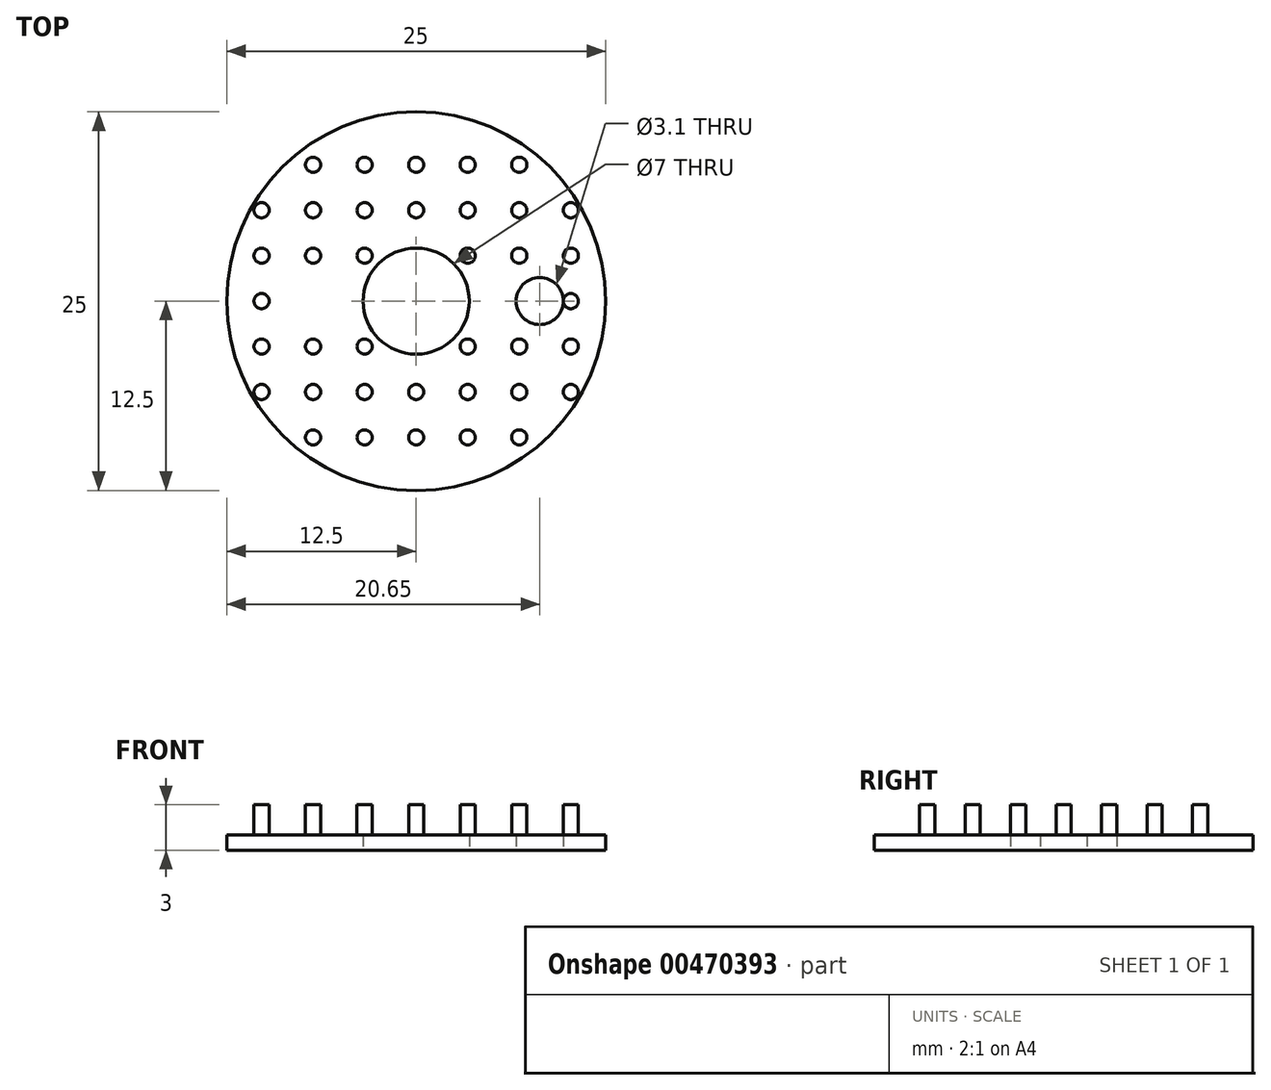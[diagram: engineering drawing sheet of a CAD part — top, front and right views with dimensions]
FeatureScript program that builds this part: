
annotation { "Feature Type Name" : "Feature", "Feature Type Description" : "" }
export const myFeature = defineFeature(function(context is Context, id is Id, definition is map)
    precondition{}
    {
        {
            var Q0;
            Q0=qCreatedBy(makeId("Top.planeOp"),FACE);
            var sketch = newSketch(context, id + "F0", { "sketchPlane" : qUnion([Q0])});
            skCircle(sketch, "E0", {"center": v(0, 0) * mm, "radius": 12.5 * mm});
            skSolve(sketch);
        }
        {
            var Q0;
            Q0=makeQuery(id+"F0.imprint","IMPRINT",FACE,{"disambiguationData":[TD([[makeQuery(id+"F0.imprint","IMPRINT",EDGE,{"derivedFrom":sQuery(id+"F0.wireOp",EDGE,"E0")}),1.0]])]});
            extrude(context, id + "F1", {"entities" : qUnion([Q0]), "depth" : 1 * mm, "offsetDistance" : 25 * mm});
        }
        {
            var Q0;
            Q0=qCreatedBy(makeId("Top.planeOp"),FACE);
            var sketch = newSketch(context, id + "F2", { "sketchPlane" : qUnion([Q0])});
            skCircle(sketch, "E1", {"center": v(-10.2, -12) * mm, "radius": 0.5 * mm});
            skLineSegment(sketch, "E2.direction1", {"start": v(-10.2, -12) * mm, "end": v(-6.8, -12) * mm, "construction": true});
            skLineSegment(sketch, "E2.direction2", {"start": v(-10.2, -12) * mm, "end": v(-10.2, -9) * mm, "construction": true});
            skCircle(sketch, "E3.0.0.1", {"center": v(-10.2, -9) * mm, "radius": 0.5 * mm});
            skCircle(sketch, "E3.0.0.2", {"center": v(-10.2, -6) * mm, "radius": 0.5 * mm});
            skCircle(sketch, "E3.0.0.3", {"center": v(-10.2, -3) * mm, "radius": 0.5 * mm});
            skCircle(sketch, "E3.0.0.4", {"center": v(-10.2, 0) * mm, "radius": 0.5 * mm});
            skCircle(sketch, "E3.0.0.5", {"center": v(-10.2, 3) * mm, "radius": 0.5 * mm});
            skCircle(sketch, "E3.0.0.6", {"center": v(-10.2, 6) * mm, "radius": 0.5 * mm});
            skCircle(sketch, "E4.0.1.0", {"center": v(-6.8, -12) * mm, "radius": 0.5 * mm});
            skCircle(sketch, "E4.0.1.1", {"center": v(-6.8, -9) * mm, "radius": 0.5 * mm});
            skCircle(sketch, "E4.0.1.2", {"center": v(-6.8, -6) * mm, "radius": 0.5 * mm});
            skCircle(sketch, "E4.0.1.3", {"center": v(-6.8, -3) * mm, "radius": 0.5 * mm});
            skCircle(sketch, "E4.0.1.4", {"center": v(-6.8, 0) * mm, "radius": 0.5 * mm});
            skCircle(sketch, "E4.0.1.5", {"center": v(-6.8, 3) * mm, "radius": 0.5 * mm});
            skCircle(sketch, "E4.0.1.6", {"center": v(-6.8, 6) * mm, "radius": 0.5 * mm});
            skCircle(sketch, "E4.0.2.1", {"center": v(-3.4, -9) * mm, "radius": 0.5 * mm});
            skCircle(sketch, "E4.0.2.2", {"center": v(-3.4, -6) * mm, "radius": 0.5 * mm});
            skCircle(sketch, "E4.0.2.3", {"center": v(-3.4, -3) * mm, "radius": 0.5 * mm});
            skCircle(sketch, "E4.0.2.4", {"center": v(-3.4, 0) * mm, "radius": 0.5 * mm});
            skCircle(sketch, "E4.0.2.5", {"center": v(-3.4, 3) * mm, "radius": 0.5 * mm});
            skCircle(sketch, "E4.0.2.6", {"center": v(-3.4, 6) * mm, "radius": 0.5 * mm});
            skCircle(sketch, "E4.0.3.1", {"center": v(0, -9) * mm, "radius": 0.5 * mm});
            skCircle(sketch, "E4.0.3.2", {"center": v(0, -6) * mm, "radius": 0.5 * mm});
            skCircle(sketch, "E4.0.3.3", {"center": v(0, -3) * mm, "radius": 0.5 * mm});
            skCircle(sketch, "E4.0.3.4", {"center": v(0, 0) * mm, "radius": 0.5 * mm});
            skCircle(sketch, "E4.0.3.5", {"center": v(0, 3) * mm, "radius": 0.5 * mm});
            skCircle(sketch, "E4.0.3.6", {"center": v(0, 6) * mm, "radius": 0.5 * mm});
            skCircle(sketch, "E4.0.4.1", {"center": v(3.4, -9) * mm, "radius": 0.5 * mm});
            skCircle(sketch, "E4.0.4.2", {"center": v(3.4, -6) * mm, "radius": 0.5 * mm});
            skCircle(sketch, "E4.0.4.3", {"center": v(3.4, -3) * mm, "radius": 0.5 * mm});
            skCircle(sketch, "E4.0.4.4", {"center": v(3.4, 0) * mm, "radius": 0.5 * mm});
            skCircle(sketch, "E4.0.4.5", {"center": v(3.4, 3) * mm, "radius": 0.5 * mm});
            skCircle(sketch, "E4.0.4.6", {"center": v(3.4, 6) * mm, "radius": 0.5 * mm});
            skCircle(sketch, "E4.0.5.1", {"center": v(6.8, -9) * mm, "radius": 0.5 * mm});
            skCircle(sketch, "E4.0.5.2", {"center": v(6.8, -6) * mm, "radius": 0.5 * mm});
            skCircle(sketch, "E4.0.5.3", {"center": v(6.8, -3) * mm, "radius": 0.5 * mm});
            skCircle(sketch, "E4.0.5.4", {"center": v(6.8, 0) * mm, "radius": 0.5 * mm});
            skCircle(sketch, "E4.0.5.5", {"center": v(6.8, 3) * mm, "radius": 0.5 * mm});
            skCircle(sketch, "E4.0.5.6", {"center": v(6.8, 6) * mm, "radius": 0.5 * mm});
            skCircle(sketch, "E4.0.6.2", {"center": v(10.2, -6) * mm, "radius": 0.5 * mm});
            skCircle(sketch, "E4.0.6.3", {"center": v(10.2, -3) * mm, "radius": 0.5 * mm});
            skCircle(sketch, "E4.0.6.4", {"center": v(10.2, 0) * mm, "radius": 0.5 * mm});
            skCircle(sketch, "E4.0.6.5", {"center": v(10.2, 3) * mm, "radius": 0.5 * mm});
            skCircle(sketch, "E4.0.6.6", {"center": v(10.2, 6) * mm, "radius": 0.5 * mm});
            skCircle(sketch, "E5.0.1.7", {"center": v(-6.8, 9) * mm, "radius": 0.5 * mm});
            skCircle(sketch, "E5.0.2.7", {"center": v(-3.4, 9) * mm, "radius": 0.5 * mm});
            skCircle(sketch, "E5.0.3.7", {"center": v(0, 9) * mm, "radius": 0.5 * mm});
            skCircle(sketch, "E5.0.4.7", {"center": v(3.4, 9) * mm, "radius": 0.5 * mm});
            skCircle(sketch, "E5.0.5.7", {"center": v(6.8, 9) * mm, "radius": 0.5 * mm});
            skSolve(sketch);
        }
        {
            var Q0;
            Q0=makeQuery(id+"F2.imprint","IMPRINT",FACE,{"disambiguationData":[TD([[makeQuery(id+"F2.imprint","IMPRINT",EDGE,{"derivedFrom":sQuery(id+"F2.wireOp",EDGE,"E4.0.6.5")}),1.0]])]});
            var Q1;
            Q1=makeQuery(id+"F2.imprint","IMPRINT",FACE,{"disambiguationData":[TD([[makeQuery(id+"F2.imprint","IMPRINT",EDGE,{"derivedFrom":sQuery(id+"F2.wireOp",EDGE,"E4.0.5.6")}),1.0]])]});
            var Q2;
            Q2=makeQuery(id+"F2.imprint","IMPRINT",FACE,{"disambiguationData":[TD([[makeQuery(id+"F2.imprint","IMPRINT",EDGE,{"derivedFrom":sQuery(id+"F2.wireOp",EDGE,"E4.0.6.4")}),1.0]])]});
            var Q3;
            Q3=makeQuery(id+"F2.imprint","IMPRINT",FACE,{"disambiguationData":[TD([[makeQuery(id+"F2.imprint","IMPRINT",EDGE,{"derivedFrom":sQuery(id+"F2.wireOp",EDGE,"E4.0.6.3")}),1.0]])]});
            var Q4;
            Q4=makeQuery(id+"F2.imprint","IMPRINT",FACE,{"disambiguationData":[TD([[makeQuery(id+"F2.imprint","IMPRINT",EDGE,{"derivedFrom":sQuery(id+"F2.wireOp",EDGE,"E4.0.5.2")}),1.0]])]});
            var Q5;
            Q5=makeQuery(id+"F2.imprint","IMPRINT",FACE,{"disambiguationData":[TD([[makeQuery(id+"F2.imprint","IMPRINT",EDGE,{"derivedFrom":sQuery(id+"F2.wireOp",EDGE,"E4.0.4.2")}),1.0]])]});
            var Q6;
            Q6=makeQuery(id+"F2.imprint","IMPRINT",FACE,{"disambiguationData":[TD([[makeQuery(id+"F2.imprint","IMPRINT",EDGE,{"derivedFrom":sQuery(id+"F2.wireOp",EDGE,"E4.0.3.2")}),1.0]])]});
            var Q7;
            Q7=makeQuery(id+"F2.imprint","IMPRINT",FACE,{"disambiguationData":[TD([[makeQuery(id+"F2.imprint","IMPRINT",EDGE,{"derivedFrom":sQuery(id+"F2.wireOp",EDGE,"E4.0.2.2")}),1.0]])]});
            var Q8;
            Q8=makeQuery(id+"F2.imprint","IMPRINT",FACE,{"disambiguationData":[TD([[makeQuery(id+"F2.imprint","IMPRINT",EDGE,{"derivedFrom":sQuery(id+"F2.wireOp",EDGE,"E4.0.1.2")}),1.0]])]});
            var Q9;
            Q9=makeQuery(id+"F2.imprint","IMPRINT",FACE,{"disambiguationData":[TD([[makeQuery(id+"F2.imprint","IMPRINT",EDGE,{"derivedFrom":sQuery(id+"F2.wireOp",EDGE,"E3.0.0.3")}),1.0]])]});
            var Q10;
            Q10=makeQuery(id+"F2.imprint","IMPRINT",FACE,{"disambiguationData":[TD([[makeQuery(id+"F2.imprint","IMPRINT",EDGE,{"derivedFrom":sQuery(id+"F2.wireOp",EDGE,"E3.0.0.4")}),1.0]])]});
            var Q11;
            Q11=makeQuery(id+"F2.imprint","IMPRINT",FACE,{"disambiguationData":[TD([[makeQuery(id+"F2.imprint","IMPRINT",EDGE,{"derivedFrom":sQuery(id+"F2.wireOp",EDGE,"E3.0.0.5")}),1.0]])]});
            var Q12;
            Q12=makeQuery(id+"F2.imprint","IMPRINT",FACE,{"disambiguationData":[TD([[makeQuery(id+"F2.imprint","IMPRINT",EDGE,{"derivedFrom":sQuery(id+"F2.wireOp",EDGE,"E4.0.1.6")}),1.0]])]});
            var Q13;
            Q13=makeQuery(id+"F2.imprint","IMPRINT",FACE,{"disambiguationData":[TD([[makeQuery(id+"F2.imprint","IMPRINT",EDGE,{"derivedFrom":sQuery(id+"F2.wireOp",EDGE,"E4.0.2.6")}),1.0]])]});
            var Q14;
            Q14=makeQuery(id+"F2.imprint","IMPRINT",FACE,{"disambiguationData":[TD([[makeQuery(id+"F2.imprint","IMPRINT",EDGE,{"derivedFrom":sQuery(id+"F2.wireOp",EDGE,"E4.0.3.6")}),1.0]])]});
            var Q15;
            Q15=makeQuery(id+"F2.imprint","IMPRINT",FACE,{"disambiguationData":[TD([[makeQuery(id+"F2.imprint","IMPRINT",EDGE,{"derivedFrom":sQuery(id+"F2.wireOp",EDGE,"E4.0.4.6")}),1.0]])]});
            var Q16;
            Q16=makeQuery(id+"F2.imprint","IMPRINT",FACE,{"disambiguationData":[TD([[makeQuery(id+"F2.imprint","IMPRINT",EDGE,{"derivedFrom":sQuery(id+"F2.wireOp",EDGE,"E4.0.1.3")}),1.0]])]});
            var Q17;
            Q17=makeQuery(id+"F2.imprint","IMPRINT",FACE,{"disambiguationData":[TD([[makeQuery(id+"F2.imprint","IMPRINT",EDGE,{"derivedFrom":sQuery(id+"F2.wireOp",EDGE,"E4.0.1.5")}),1.0]])]});
            var Q18;
            Q18=makeQuery(id+"F2.imprint","IMPRINT",FACE,{"disambiguationData":[TD([[makeQuery(id+"F2.imprint","IMPRINT",EDGE,{"derivedFrom":sQuery(id+"F2.wireOp",EDGE,"E4.0.2.3")}),1.0]])]});
            var Q19;
            Q19=makeQuery(id+"F2.imprint","IMPRINT",FACE,{"disambiguationData":[TD([[makeQuery(id+"F2.imprint","IMPRINT",EDGE,{"derivedFrom":sQuery(id+"F2.wireOp",EDGE,"E4.0.2.5")}),1.0]])]});
            var Q20;
            Q20=makeQuery(id+"F2.imprint","IMPRINT",FACE,{"disambiguationData":[TD([[makeQuery(id+"F2.imprint","IMPRINT",EDGE,{"derivedFrom":sQuery(id+"F2.wireOp",EDGE,"E4.0.5.3")}),1.0]])]});
            var Q21;
            Q21=makeQuery(id+"F2.imprint","IMPRINT",FACE,{"disambiguationData":[TD([[makeQuery(id+"F2.imprint","IMPRINT",EDGE,{"derivedFrom":sQuery(id+"F2.wireOp",EDGE,"E4.0.4.3")}),1.0]])]});
            var Q22;
            Q22=makeQuery(id+"F2.imprint","IMPRINT",FACE,{"disambiguationData":[TD([[makeQuery(id+"F2.imprint","IMPRINT",EDGE,{"derivedFrom":sQuery(id+"F2.wireOp",EDGE,"E4.0.5.5")}),1.0]])]});
            var Q23;
            Q23=makeQuery(id+"F2.imprint","IMPRINT",FACE,{"disambiguationData":[TD([[makeQuery(id+"F2.imprint","IMPRINT",EDGE,{"derivedFrom":sQuery(id+"F2.wireOp",EDGE,"E4.0.4.5")}),1.0]])]});
            var Q24;
            Q24=makeQuery(id+"F2.imprint","IMPRINT",FACE,{"disambiguationData":[TD([[makeQuery(id+"F2.imprint","IMPRINT",EDGE,{"derivedFrom":sQuery(id+"F2.wireOp",EDGE,"E5.0.5.7")}),1.0]])]});
            var Q25;
            Q25=makeQuery(id+"F2.imprint","IMPRINT",FACE,{"disambiguationData":[TD([[makeQuery(id+"F2.imprint","IMPRINT",EDGE,{"derivedFrom":sQuery(id+"F2.wireOp",EDGE,"E5.0.4.7")}),1.0]])]});
            var Q26;
            Q26=makeQuery(id+"F2.imprint","IMPRINT",FACE,{"disambiguationData":[TD([[makeQuery(id+"F2.imprint","IMPRINT",EDGE,{"derivedFrom":sQuery(id+"F2.wireOp",EDGE,"E5.0.3.7")}),1.0]])]});
            var Q27;
            Q27=makeQuery(id+"F2.imprint","IMPRINT",FACE,{"disambiguationData":[TD([[makeQuery(id+"F2.imprint","IMPRINT",EDGE,{"derivedFrom":sQuery(id+"F2.wireOp",EDGE,"E5.0.2.7")}),1.0]])]});
            var Q28;
            Q28=makeQuery(id+"F2.imprint","IMPRINT",FACE,{"disambiguationData":[TD([[makeQuery(id+"F2.imprint","IMPRINT",EDGE,{"derivedFrom":sQuery(id+"F2.wireOp",EDGE,"E5.0.1.7")}),1.0]])]});
            var Q29;
            Q29=makeQuery(id+"F2.imprint","IMPRINT",FACE,{"disambiguationData":[TD([[makeQuery(id+"F2.imprint","IMPRINT",EDGE,{"derivedFrom":sQuery(id+"F2.wireOp",EDGE,"E4.0.6.6")}),1.0]])]});
            var Q30;
            Q30=makeQuery(id+"F2.imprint","IMPRINT",FACE,{"disambiguationData":[TD([[makeQuery(id+"F2.imprint","IMPRINT",EDGE,{"derivedFrom":sQuery(id+"F2.wireOp",EDGE,"E4.0.5.1")}),1.0]])]});
            var Q31;
            Q31=makeQuery(id+"F2.imprint","IMPRINT",FACE,{"disambiguationData":[TD([[makeQuery(id+"F2.imprint","IMPRINT",EDGE,{"derivedFrom":sQuery(id+"F2.wireOp",EDGE,"E4.0.4.1")}),1.0]])]});
            var Q32;
            Q32=makeQuery(id+"F2.imprint","IMPRINT",FACE,{"disambiguationData":[TD([[makeQuery(id+"F2.imprint","IMPRINT",EDGE,{"derivedFrom":sQuery(id+"F2.wireOp",EDGE,"E3.0.0.6")}),1.0]])]});
            var Q33;
            Q33=makeQuery(id+"F2.imprint","IMPRINT",FACE,{"disambiguationData":[TD([[makeQuery(id+"F2.imprint","IMPRINT",EDGE,{"derivedFrom":sQuery(id+"F2.wireOp",EDGE,"E4.0.6.2")}),1.0]])]});
            var Q34;
            Q34=makeQuery(id+"F2.imprint","IMPRINT",FACE,{"disambiguationData":[TD([[makeQuery(id+"F2.imprint","IMPRINT",EDGE,{"derivedFrom":sQuery(id+"F2.wireOp",EDGE,"E4.0.2.1")}),1.0]])]});
            var Q35;
            Q35=makeQuery(id+"F2.imprint","IMPRINT",FACE,{"disambiguationData":[TD([[makeQuery(id+"F2.imprint","IMPRINT",EDGE,{"derivedFrom":sQuery(id+"F2.wireOp",EDGE,"E4.0.3.1")}),1.0]])]});
            var Q36;
            Q36=makeQuery(id+"F2.imprint","IMPRINT",FACE,{"disambiguationData":[TD([[makeQuery(id+"F2.imprint","IMPRINT",EDGE,{"derivedFrom":sQuery(id+"F2.wireOp",EDGE,"E4.0.1.1")}),1.0]])]});
            var Q37;
            Q37=makeQuery(id+"F2.imprint","IMPRINT",FACE,{"disambiguationData":[TD([[makeQuery(id+"F2.imprint","IMPRINT",EDGE,{"derivedFrom":sQuery(id+"F2.wireOp",EDGE,"E3.0.0.2")}),1.0]])]});
            extrude(context, id + "F3", {"entities" : qUnion([Q0, Q1, Q2, Q3, Q4, Q5, Q6, Q7, Q8, Q9, Q10, Q11, Q12, Q13, Q14, Q15, Q16, Q17, Q18, Q19, Q20, Q21, Q22, Q23, Q24, Q25, Q26, Q27, Q28, Q29, Q30, Q31, Q32, Q33, Q34, Q35, Q36, Q37]), "operationType" : NewBodyOperationType.ADD, "depth" : 3 * mm, "offsetDistance" : 25 * mm});
        }
        {
            var Q0;
            Q0=qCreatedBy(makeId("Top.planeOp"),FACE);
            var sketch = newSketch(context, id + "F4", { "sketchPlane" : qUnion([Q0])});
            skCircle(sketch, "E6", {"center": v(0, 0) * mm, "radius": 3.5 * mm});
            skCircle(sketch, "E7", {"center": v(8.15, 0) * mm, "radius": 1.55 * mm});
            skLineSegment(sketch, "E8", {"start": v(0, 0) * mm, "end": v(0, -0.97) * mm, "construction": true});
            skCircle(sketch, "E9.MirrorC", {"center": v(-8.15, 0) * mm, "radius": 1.55 * mm});
            skSolve(sketch);
        }
        {
            var Q0;
            Q0=makeQuery(id+"F4.imprint","IMPRINT",FACE,{"disambiguationData":[TD([[makeQuery(id+"F4.imprint","IMPRINT",EDGE,{"derivedFrom":sQuery(id+"F4.wireOp",EDGE,"E6")}),1.0]])]});
            var Q1;
            Q1=makeQuery(id+"F4.imprint","IMPRINT",FACE,{"disambiguationData":[TD([[makeQuery(id+"F4.imprint","IMPRINT",EDGE,{"derivedFrom":sQuery(id+"F4.wireOp",EDGE,"E7")}),1.0]])]});
            var Q2;
            Q2=makeQuery(id+"F4.imprint","IMPRINT",FACE,{"disambiguationData":[TD([[makeQuery(id+"F4.imprint","IMPRINT",EDGE,{"derivedFrom":sQuery(id+"F4.wireOp",EDGE,"E9.MirrorC")}),-1.0]])]});
            extrude(context, id + "F5", {"entities" : qUnion([Q0, Q1, Q2]), "operationType" : NewBodyOperationType.REMOVE, "endBound" : BoundingType.THROUGH_ALL, "depth" : 25 * mm, "offsetDistance" : 25 * mm});
        }
    });
